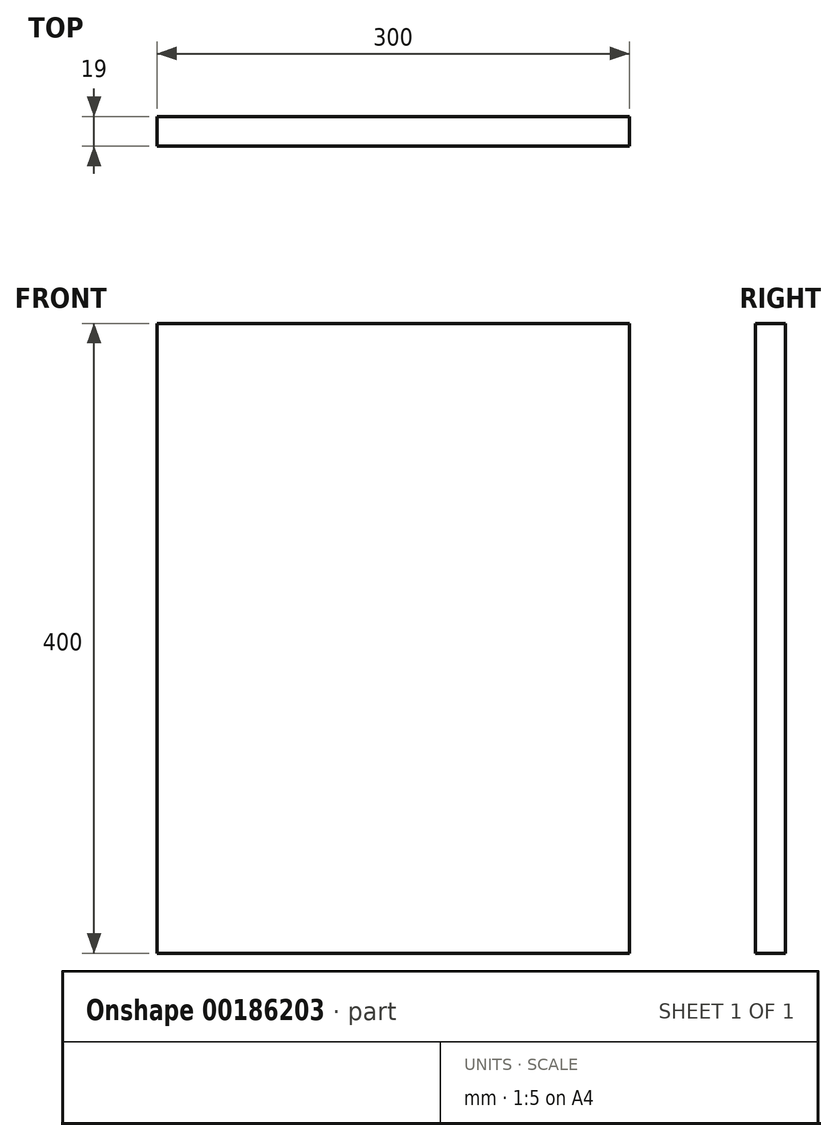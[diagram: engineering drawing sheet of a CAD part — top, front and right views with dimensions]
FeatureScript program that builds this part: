
annotation { "Feature Type Name" : "Feature", "Feature Type Description" : "" }
export const myFeature = defineFeature(function(context is Context, id is Id, definition is map)
    precondition{}
    {
        {
            var Q0;
            Q0=qCreatedBy(makeId("Front.planeOp"),FACE);
            var sketch = newSketch(context, id + "F0", { "sketchPlane" : qUnion([Q0])});
            skLineSegment(sketch, "E0.bottom", {"start": v(-103.69, 220.86) * mm, "end": v(196.31, 220.86) * mm});
            skLineSegment(sketch, "E0.top", {"start": v(-103.69, -179.14) * mm, "end": v(196.31, -179.14) * mm});
            skLineSegment(sketch, "E0.left", {"start": v(-103.69, 220.86) * mm, "end": v(-103.69, -179.14) * mm});
            skLineSegment(sketch, "E0.right", {"start": v(196.31, 220.86) * mm, "end": v(196.31, -179.14) * mm});
            skSolve(sketch);
        }
        {
            var Q0;
            Q0 = qSketchRegion(id + "F0", true);
            extrude(context, id + "F1", {"entities" : qUnion([Q0]), "depth" : 19 * mm});
        }
    });
